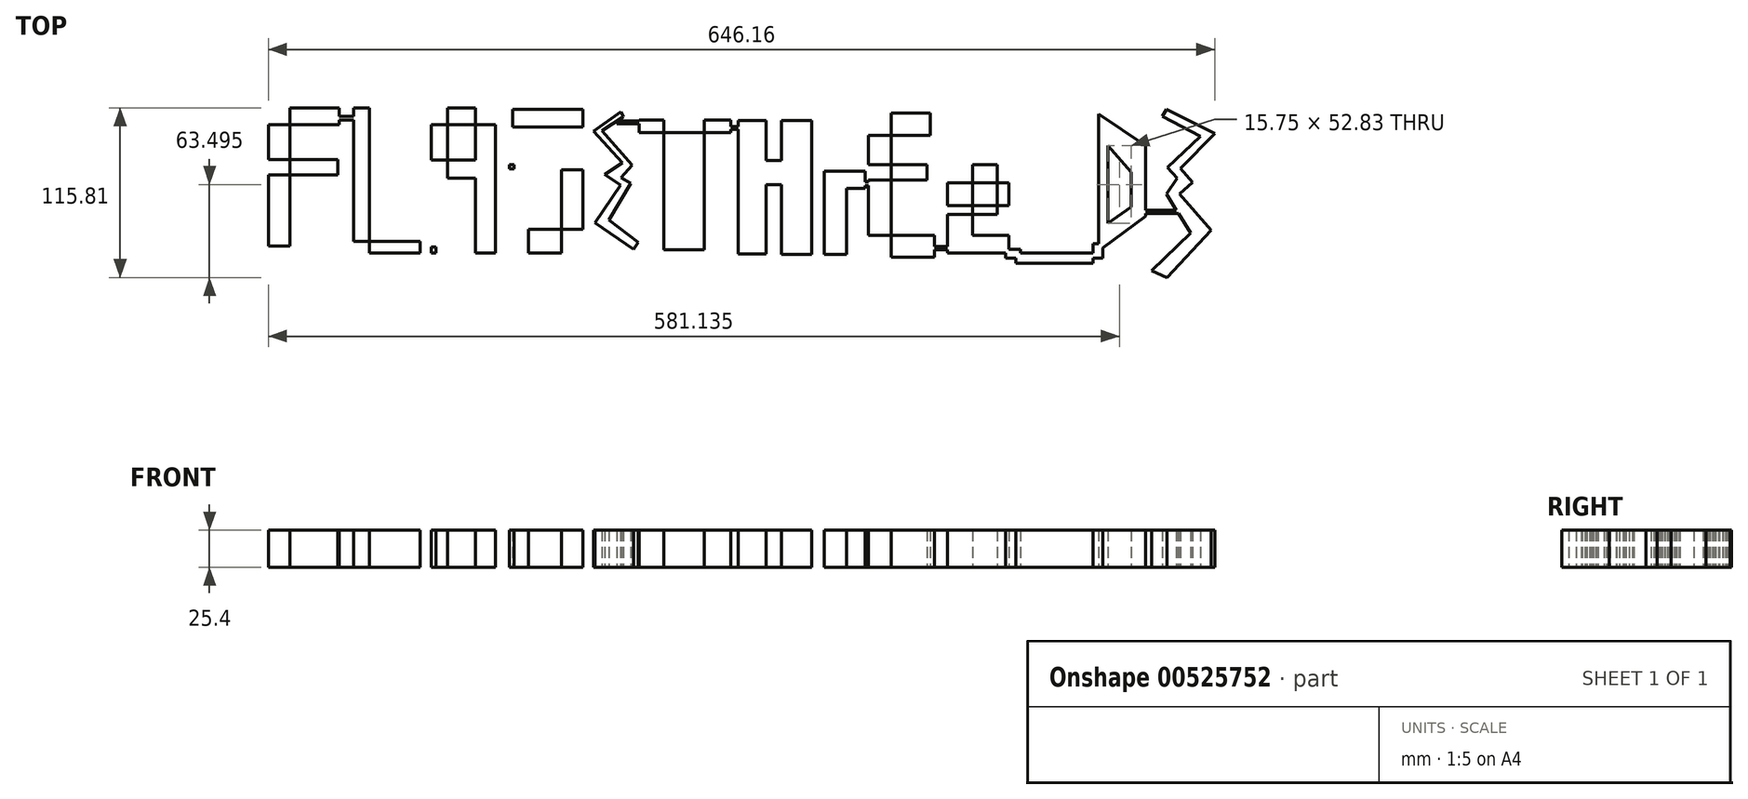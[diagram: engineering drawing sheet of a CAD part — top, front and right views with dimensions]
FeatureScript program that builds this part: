
annotation { "Feature Type Name" : "Feature", "Feature Type Description" : "" }
export const myFeature = defineFeature(function(context is Context, id is Id, definition is map)
    precondition{}
    {
        {
            var Q0;
            Q0=qCreatedBy(makeId("Top.planeOp"),FACE);
            var sketch = newSketch(context, id + "F0", { "sketchPlane" : qUnion([Q0])});
            skLineSegment(sketch, "E0.bottom", {"start": v(-64.83, -35.83) * mm, "end": v(-49.93, -35.83) * mm});
            skLineSegment(sketch, "E0.top", {"start": v(-64.83, 58.64) * mm, "end": v(-49.93, 58.64) * mm});
            skLineSegment(sketch, "E0.left", {"start": v(-64.83, -35.83) * mm, "end": v(-64.83, 58.64) * mm});
            skLineSegment(sketch, "E0.right", {"start": v(-49.93, -35.83) * mm, "end": v(-49.93, 58.64) * mm});
            skLineSegment(sketch, "E1.bottom", {"start": v(-64.83, 58.64) * mm, "end": v(-16.34, 58.64) * mm});
            skLineSegment(sketch, "E1.top", {"start": v(-64.83, 47.14) * mm, "end": v(-16.34, 47.14) * mm});
            skLineSegment(sketch, "E1.left", {"start": v(-64.83, 58.64) * mm, "end": v(-64.83, 47.14) * mm});
            skLineSegment(sketch, "E1.right", {"start": v(-16.34, 58.64) * mm, "end": v(-16.34, 47.14) * mm});
            skLineSegment(sketch, "E2.bottom", {"start": v(-64.83, 23.44) * mm, "end": v(-17.24, 23.44) * mm});
            skLineSegment(sketch, "E2.top", {"start": v(-64.83, 12.84) * mm, "end": v(-17.24, 12.84) * mm});
            skLineSegment(sketch, "E2.left", {"start": v(-64.83, 23.44) * mm, "end": v(-64.83, 12.84) * mm});
            skLineSegment(sketch, "E2.right", {"start": v(-17.24, 23.44) * mm, "end": v(-17.24, 12.84) * mm});
            skLineSegment(sketch, "E3.bottom", {"start": v(-6.65, 58.64) * mm, "end": v(4.31, 58.64) * mm});
            skLineSegment(sketch, "E3.top", {"start": v(-6.65, -40.32) * mm, "end": v(4.31, -40.32) * mm});
            skLineSegment(sketch, "E3.left", {"start": v(-6.65, 58.64) * mm, "end": v(-6.65, -40.32) * mm});
            skLineSegment(sketch, "E3.right", {"start": v(4.31, 58.64) * mm, "end": v(4.31, -40.32) * mm});
            skLineSegment(sketch, "E4.bottom", {"start": v(-6.65, -40.32) * mm, "end": v(38.97, -40.32) * mm});
            skLineSegment(sketch, "E4.top", {"start": v(-6.65, -32.6) * mm, "end": v(38.97, -32.6) * mm});
            skLineSegment(sketch, "E4.left", {"start": v(-6.65, -40.32) * mm, "end": v(-6.65, -32.6) * mm});
            skLineSegment(sketch, "E4.right", {"start": v(38.97, -40.32) * mm, "end": v(38.97, -32.6) * mm});
            skLineSegment(sketch, "E5.bottom", {"start": v(46.34, -40.32) * mm, "end": v(57.47, -40.32) * mm});
            skLineSegment(sketch, "E5.top", {"start": v(46.34, 58.64) * mm, "end": v(57.47, 58.64) * mm});
            skLineSegment(sketch, "E5.left", {"start": v(46.34, -40.32) * mm, "end": v(46.34, 58.64) * mm});
            skLineSegment(sketch, "E5.right", {"start": v(57.47, -40.32) * mm, "end": v(57.47, 58.64) * mm});
            skLineSegment(sketch, "E6.bottom", {"start": v(46.34, 58.64) * mm, "end": v(90.34, 58.64) * mm});
            skLineSegment(sketch, "E6.top", {"start": v(46.34, 47.32) * mm, "end": v(90.34, 47.32) * mm});
            skLineSegment(sketch, "E6.left", {"start": v(46.34, 58.64) * mm, "end": v(46.34, 47.32) * mm});
            skLineSegment(sketch, "E6.right", {"start": v(90.34, 58.64) * mm, "end": v(90.34, 47.32) * mm});
            skLineSegment(sketch, "E7.bottom", {"start": v(90.34, 58.64) * mm, "end": v(76.5, 58.64) * mm});
            skLineSegment(sketch, "E7.top", {"start": v(90.34, -40.32) * mm, "end": v(76.5, -40.32) * mm});
            skLineSegment(sketch, "E7.left", {"start": v(90.34, 58.64) * mm, "end": v(90.34, -40.32) * mm});
            skLineSegment(sketch, "E7.right", {"start": v(76.5, 58.64) * mm, "end": v(76.5, -40.32) * mm});
            skLineSegment(sketch, "E8.bottom", {"start": v(46.34, 23.08) * mm, "end": v(90.34, 23.08) * mm});
            skLineSegment(sketch, "E8.top", {"start": v(46.34, 10.69) * mm, "end": v(90.34, 10.69) * mm});
            skLineSegment(sketch, "E8.left", {"start": v(46.34, 23.08) * mm, "end": v(46.34, 10.69) * mm});
            skLineSegment(sketch, "E8.right", {"start": v(90.34, 23.08) * mm, "end": v(90.34, 10.69) * mm});
            skLineSegment(sketch, "E9.bottom", {"start": v(99.74, 57.74) * mm, "end": v(112.67, 57.74) * mm});
            skLineSegment(sketch, "E9.top", {"start": v(99.74, -40.5) * mm, "end": v(112.67, -40.5) * mm});
            skLineSegment(sketch, "E9.left", {"start": v(99.74, 57.74) * mm, "end": v(99.74, -40.5) * mm});
            skLineSegment(sketch, "E9.right", {"start": v(112.67, 57.74) * mm, "end": v(112.67, -40.5) * mm});
            skLineSegment(sketch, "E10.bottom", {"start": v(99.74, -40.5) * mm, "end": v(149.85, -40.5) * mm});
            skLineSegment(sketch, "E10.top", {"start": v(99.74, -24.16) * mm, "end": v(149.85, -24.16) * mm});
            skLineSegment(sketch, "E10.left", {"start": v(99.74, -40.5) * mm, "end": v(99.74, -24.16) * mm});
            skLineSegment(sketch, "E10.right", {"start": v(149.85, -40.5) * mm, "end": v(149.85, -24.16) * mm});
            skLineSegment(sketch, "E11.bottom", {"start": v(149.85, -40.5) * mm, "end": v(135.3, -40.5) * mm});
            skLineSegment(sketch, "E11.top", {"start": v(149.85, 16.43) * mm, "end": v(135.3, 16.43) * mm});
            skLineSegment(sketch, "E11.left", {"start": v(149.85, -40.5) * mm, "end": v(149.85, 16.43) * mm});
            skLineSegment(sketch, "E11.right", {"start": v(135.3, -40.5) * mm, "end": v(135.3, 16.43) * mm});
            skLineSegment(sketch, "E12.bottom", {"start": v(101.9, 57.74) * mm, "end": v(149.85, 57.74) * mm});
            skLineSegment(sketch, "E12.top", {"start": v(101.9, 45.7) * mm, "end": v(149.85, 45.7) * mm});
            skLineSegment(sketch, "E12.left", {"start": v(101.9, 57.74) * mm, "end": v(101.9, 45.7) * mm});
            skLineSegment(sketch, "E12.right", {"start": v(149.85, 57.74) * mm, "end": v(149.85, 45.7) * mm});
            skLineSegment(sketch, "E13", {"start": v(176.04, 56.16) * mm, "end": v(157.37, 42.57) * mm});
            skLineSegment(sketch, "E14", {"start": v(157.37, 42.57) * mm, "end": v(177.05, 20.98) * mm});
            skLineSegment(sketch, "E15", {"start": v(177.05, 20.98) * mm, "end": v(164.86, 13.11) * mm});
            skLineSegment(sketch, "E16", {"start": v(164.86, 13.11) * mm, "end": v(175.65, 5.74) * mm});
            skLineSegment(sketch, "E17", {"start": v(175.65, 5.74) * mm, "end": v(158.17, -19.88) * mm});
            skLineSegment(sketch, "E18", {"start": v(158.17, -19.88) * mm, "end": v(184.46, -37.82) * mm});
            skLineSegment(sketch, "E19", {"start": v(184.46, -37.82) * mm, "end": v(187.69, -33.1) * mm});
            skLineSegment(sketch, "E20", {"start": v(187.69, -33.1) * mm, "end": v(167.65, -17.88) * mm});
            skLineSegment(sketch, "E21", {"start": v(167.65, -17.88) * mm, "end": v(182.51, 7.27) * mm});
            skLineSegment(sketch, "E22", {"start": v(182.51, 7.27) * mm, "end": v(175.99, 11.12) * mm});
            skLineSegment(sketch, "E23", {"start": v(175.99, 11.12) * mm, "end": v(183.66, 19.59) * mm});
            skLineSegment(sketch, "E24", {"start": v(183.66, 19.59) * mm, "end": v(163.08, 42.95) * mm});
            skLineSegment(sketch, "E25", {"start": v(163.08, 42.95) * mm, "end": v(177.69, 52.6) * mm});
            skLineSegment(sketch, "E26", {"start": v(177.69, 52.6) * mm, "end": v(176.04, 56.16) * mm});
            skLineSegment(sketch, "E27.bottom", {"start": v(188.24, 50.3) * mm, "end": v(251.03, 50.3) * mm});
            skLineSegment(sketch, "E27.top", {"start": v(188.24, 41.76) * mm, "end": v(251.03, 41.76) * mm});
            skLineSegment(sketch, "E27.left", {"start": v(188.24, 50.3) * mm, "end": v(188.24, 41.76) * mm});
            skLineSegment(sketch, "E27.right", {"start": v(251.03, 50.3) * mm, "end": v(251.03, 41.76) * mm});
            skLineSegment(sketch, "E28.bottom", {"start": v(205.11, 50.3) * mm, "end": v(232.66, 50.3) * mm});
            skLineSegment(sketch, "E28.top", {"start": v(205.11, -38.33) * mm, "end": v(232.66, -38.33) * mm});
            skLineSegment(sketch, "E28.left", {"start": v(205.11, 50.3) * mm, "end": v(205.11, -38.33) * mm});
            skLineSegment(sketch, "E28.right", {"start": v(232.66, 50.3) * mm, "end": v(232.66, -38.33) * mm});
            skLineSegment(sketch, "E29.bottom", {"start": v(255.94, 49.88) * mm, "end": v(275.16, 49.88) * mm});
            skLineSegment(sketch, "E29.top", {"start": v(255.94, -41.1) * mm, "end": v(275.16, -41.1) * mm});
            skLineSegment(sketch, "E29.left", {"start": v(255.94, 49.88) * mm, "end": v(255.94, -41.1) * mm});
            skLineSegment(sketch, "E29.right", {"start": v(275.16, 49.88) * mm, "end": v(275.16, -41.1) * mm});
            skLineSegment(sketch, "E30.bottom", {"start": v(262.35, 22.75) * mm, "end": v(298.66, 22.75) * mm});
            skLineSegment(sketch, "E30.top", {"start": v(262.35, 6.3) * mm, "end": v(298.66, 6.3) * mm});
            skLineSegment(sketch, "E30.left", {"start": v(262.35, 22.75) * mm, "end": v(262.35, 6.3) * mm});
            skLineSegment(sketch, "E30.right", {"start": v(298.66, 22.75) * mm, "end": v(298.66, 6.3) * mm});
            skLineSegment(sketch, "E31.bottom", {"start": v(285.63, 50.1) * mm, "end": v(306.13, 50.1) * mm});
            skLineSegment(sketch, "E31.top", {"start": v(285.63, -41.53) * mm, "end": v(306.13, -41.53) * mm});
            skLineSegment(sketch, "E31.left", {"start": v(285.63, 50.1) * mm, "end": v(285.63, -41.53) * mm});
            skLineSegment(sketch, "E31.right", {"start": v(306.13, 50.1) * mm, "end": v(306.13, -41.53) * mm});
            skLineSegment(sketch, "E32.bottom", {"start": v(330.05, -41.53) * mm, "end": v(314.9, -41.53) * mm});
            skLineSegment(sketch, "E32.top", {"start": v(330.05, 15.28) * mm, "end": v(314.9, 15.28) * mm});
            skLineSegment(sketch, "E32.left", {"start": v(330.05, -41.53) * mm, "end": v(330.05, 15.28) * mm});
            skLineSegment(sketch, "E32.right", {"start": v(314.9, -41.53) * mm, "end": v(314.9, 15.28) * mm});
            skLineSegment(sketch, "E33.bottom", {"start": v(314.9, 15.28) * mm, "end": v(342.66, 15.28) * mm});
            skLineSegment(sketch, "E33.top", {"start": v(314.9, 3.53) * mm, "end": v(342.66, 3.53) * mm});
            skLineSegment(sketch, "E33.left", {"start": v(314.9, 15.28) * mm, "end": v(314.9, 3.53) * mm});
            skLineSegment(sketch, "E33.right", {"start": v(342.66, 15.28) * mm, "end": v(342.66, 3.53) * mm});
            skLineSegment(sketch, "E34.bottom", {"start": v(344.8, 55) * mm, "end": v(360.38, 55) * mm});
            skLineSegment(sketch, "E34.top", {"start": v(344.8, -43.46) * mm, "end": v(360.38, -43.46) * mm});
            skLineSegment(sketch, "E34.left", {"start": v(344.8, 55) * mm, "end": v(344.8, -43.46) * mm});
            skLineSegment(sketch, "E34.right", {"start": v(360.38, 55) * mm, "end": v(360.38, -43.46) * mm});
            skLineSegment(sketch, "E35.bottom", {"start": v(344.8, 55) * mm, "end": v(387.08, 55) * mm});
            skLineSegment(sketch, "E35.top", {"start": v(344.8, 39.84) * mm, "end": v(387.08, 39.84) * mm});
            skLineSegment(sketch, "E35.left", {"start": v(344.8, 55) * mm, "end": v(344.8, 39.84) * mm});
            skLineSegment(sketch, "E35.right", {"start": v(387.08, 55) * mm, "end": v(387.08, 39.84) * mm});
            skLineSegment(sketch, "E36.bottom", {"start": v(344.8, 19.76) * mm, "end": v(384.94, 19.76) * mm});
            skLineSegment(sketch, "E36.top", {"start": v(344.8, 9.51) * mm, "end": v(384.94, 9.51) * mm});
            skLineSegment(sketch, "E36.left", {"start": v(344.8, 19.76) * mm, "end": v(344.8, 9.51) * mm});
            skLineSegment(sketch, "E36.right", {"start": v(384.94, 19.76) * mm, "end": v(384.94, 9.51) * mm});
            skLineSegment(sketch, "E37.bottom", {"start": v(344.8, -43.46) * mm, "end": v(389.86, -43.46) * mm});
            skLineSegment(sketch, "E37.top", {"start": v(344.8, -28.3) * mm, "end": v(389.86, -28.3) * mm});
            skLineSegment(sketch, "E37.left", {"start": v(344.8, -43.46) * mm, "end": v(344.8, -28.3) * mm});
            skLineSegment(sketch, "E37.right", {"start": v(389.86, -43.46) * mm, "end": v(389.86, -28.3) * mm});
            skLineSegment(sketch, "E38.bottom", {"start": v(415.91, -40.47) * mm, "end": v(398.83, -40.47) * mm});
            skLineSegment(sketch, "E38.top", {"start": v(415.91, 19.76) * mm, "end": v(398.83, 19.76) * mm});
            skLineSegment(sketch, "E38.left", {"start": v(415.91, -40.47) * mm, "end": v(415.91, 19.76) * mm});
            skLineSegment(sketch, "E38.right", {"start": v(398.83, -40.47) * mm, "end": v(398.83, 19.76) * mm});
            skLineSegment(sketch, "E39.bottom", {"start": v(398.83, 19.76) * mm, "end": v(440.9, 19.76) * mm});
            skLineSegment(sketch, "E39.top", {"start": v(398.83, 7.59) * mm, "end": v(440.9, 7.59) * mm});
            skLineSegment(sketch, "E39.left", {"start": v(398.83, 19.76) * mm, "end": v(398.83, 7.59) * mm});
            skLineSegment(sketch, "E39.right", {"start": v(440.9, 19.76) * mm, "end": v(440.9, 7.59) * mm});
            skLineSegment(sketch, "E40.bottom", {"start": v(440.9, 19.76) * mm, "end": v(432.78, 19.76) * mm});
            skLineSegment(sketch, "E40.top", {"start": v(440.9, -13.98) * mm, "end": v(432.78, -13.98) * mm});
            skLineSegment(sketch, "E40.left", {"start": v(440.9, 19.76) * mm, "end": v(440.9, -13.98) * mm});
            skLineSegment(sketch, "E40.right", {"start": v(432.78, 19.76) * mm, "end": v(432.78, -13.98) * mm});
            skLineSegment(sketch, "E41.bottom", {"start": v(440.9, -13.98) * mm, "end": v(398.83, -13.98) * mm});
            skLineSegment(sketch, "E41.top", {"start": v(440.9, -8) * mm, "end": v(398.83, -8) * mm});
            skLineSegment(sketch, "E41.left", {"start": v(440.9, -13.98) * mm, "end": v(440.9, -8) * mm});
            skLineSegment(sketch, "E41.right", {"start": v(398.83, -13.98) * mm, "end": v(398.83, -8) * mm});
            skLineSegment(sketch, "E42.bottom", {"start": v(398.83, -40.47) * mm, "end": v(440.9, -40.47) * mm});
            skLineSegment(sketch, "E42.top", {"start": v(398.83, -28.3) * mm, "end": v(440.9, -28.3) * mm});
            skLineSegment(sketch, "E42.left", {"start": v(398.83, -40.47) * mm, "end": v(398.83, -28.3) * mm});
            skLineSegment(sketch, "E42.right", {"start": v(440.9, -40.47) * mm, "end": v(440.9, -28.3) * mm});
            skPoint(sketch, "E43.firstSnap0", {"position": v(419.86, -40.47) * mm});
            skLineSegment(sketch, "E43.bottom", {"start": v(445.44, -40.47) * mm, "end": v(498.27, -40.47) * mm});
            skLineSegment(sketch, "E43.top", {"start": v(445.44, -47.52) * mm, "end": v(498.27, -47.52) * mm});
            skLineSegment(sketch, "E43.left", {"start": v(445.44, -40.47) * mm, "end": v(445.44, -47.52) * mm});
            skLineSegment(sketch, "E43.right", {"start": v(498.27, -40.47) * mm, "end": v(498.27, -47.52) * mm});
            skLineSegment(sketch, "E44", {"start": v(502.08, -39.14) * mm, "end": v(502.08, 54.33) * mm});
            skLineSegment(sketch, "E45", {"start": v(502.08, 54.33) * mm, "end": v(534.08, 32.74) * mm});
            skLineSegment(sketch, "E46", {"start": v(534.08, 32.74) * mm, "end": v(534.08, -15.52) * mm});
            skLineSegment(sketch, "E47", {"start": v(534.08, -15.52) * mm, "end": v(502.08, -39.14) * mm});
            skLineSegment(sketch, "E48", {"start": v(508.43, -20.09) * mm, "end": v(508.43, 32.74) * mm});
            skLineSegment(sketch, "E49", {"start": v(508.43, 32.74) * mm, "end": v(524.18, 14.7) * mm});
            skLineSegment(sketch, "E50", {"start": v(524.18, 14.7) * mm, "end": v(524.18, -8.91) * mm});
            skLineSegment(sketch, "E51", {"start": v(508.43, -20.09) * mm, "end": v(524.18, -8.91) * mm});
            skLineSegment(sketch, "E52", {"start": v(545.51, 52.8) * mm, "end": v(571.67, 39.34) * mm});
            skLineSegment(sketch, "E53", {"start": v(571.67, 39.34) * mm, "end": v(549.07, 18) * mm});
            skLineSegment(sketch, "E54", {"start": v(549.07, 18) * mm, "end": v(555.86, 10.8) * mm});
            skLineSegment(sketch, "E55", {"start": v(555.86, 10.8) * mm, "end": v(548.3, 0) * mm});
            skLineSegment(sketch, "E56", {"start": v(548.3, 0) * mm, "end": v(564.82, -26.95) * mm});
            skLineSegment(sketch, "E57", {"start": v(564.82, -26.95) * mm, "end": v(538.4, -52.6) * mm});
            skLineSegment(sketch, "E58", {"start": v(538.4, -52.6) * mm, "end": v(548.82, -57.17) * mm});
            skLineSegment(sketch, "E59", {"start": v(548.82, -57.17) * mm, "end": v(579.04, -24.92) * mm});
            skLineSegment(sketch, "E60", {"start": v(579.04, -24.92) * mm, "end": v(557.45, 0) * mm});
            skLineSegment(sketch, "E61", {"start": v(557.45, 0) * mm, "end": v(566.3, 7.67) * mm});
            skLineSegment(sketch, "E62", {"start": v(566.3, 7.67) * mm, "end": v(557.83, 17.46) * mm});
            skLineSegment(sketch, "E63", {"start": v(557.83, 17.46) * mm, "end": v(581.33, 41.12) * mm});
            skLineSegment(sketch, "E64", {"start": v(581.33, 41.12) * mm, "end": v(548.56, 57.63) * mm});
            skLineSegment(sketch, "E65", {"start": v(548.56, 57.63) * mm, "end": v(545.51, 52.8) * mm});
            skPoint(sketch, "E66.firstSnap0", {"position": v(-16.34, 52.9) * mm});
            skLineSegment(sketch, "E66.bottom", {"start": v(-19.12, 52.9) * mm, "end": v(-3.22, 52.9) * mm});
            skLineSegment(sketch, "E66.top", {"start": v(-19.12, 50.27) * mm, "end": v(-3.22, 50.27) * mm});
            skLineSegment(sketch, "E66.left", {"start": v(-19.12, 52.9) * mm, "end": v(-19.12, 50.27) * mm});
            skLineSegment(sketch, "E66.right", {"start": v(-3.22, 52.9) * mm, "end": v(-3.22, 50.27) * mm});
            skLineSegment(sketch, "E67.bottom", {"start": v(38.97, -36.46) * mm, "end": v(49.7, -36.46) * mm});
            skLineSegment(sketch, "E67.top", {"start": v(38.97, -40.32) * mm, "end": v(49.7, -40.32) * mm});
            skLineSegment(sketch, "E67.left", {"start": v(38.97, -36.46) * mm, "end": v(38.97, -40.32) * mm});
            skLineSegment(sketch, "E67.right", {"start": v(49.7, -36.46) * mm, "end": v(49.7, -40.32) * mm});
            skLineSegment(sketch, "E68.bottom", {"start": v(87.25, 19.77) * mm, "end": v(102.9, 19.77) * mm});
            skLineSegment(sketch, "E68.top", {"start": v(87.25, 16.9) * mm, "end": v(102.9, 16.9) * mm});
            skLineSegment(sketch, "E68.left", {"start": v(87.25, 19.77) * mm, "end": v(87.25, 16.9) * mm});
            skLineSegment(sketch, "E68.right", {"start": v(102.9, 19.77) * mm, "end": v(102.9, 16.9) * mm});
            skLineSegment(sketch, "E69.bottom", {"start": v(149.85, -18.56) * mm, "end": v(163.12, -18.56) * mm});
            skLineSegment(sketch, "E69.top", {"start": v(149.85, -20.12) * mm, "end": v(163.12, -20.12) * mm});
            skLineSegment(sketch, "E69.left", {"start": v(149.85, -18.56) * mm, "end": v(149.85, -20.12) * mm});
            skLineSegment(sketch, "E69.right", {"start": v(163.12, -18.56) * mm, "end": v(163.12, -20.12) * mm});
            skPoint(sketch, "E70.oppositeSnap0", {"position": v(170.38, 47.78) * mm});
            skLineSegment(sketch, "E70.bottom", {"start": v(173.25, 49.67) * mm, "end": v(192.06, 49.67) * mm});
            skLineSegment(sketch, "E70.top", {"start": v(173.25, 47.78) * mm, "end": v(192.06, 47.78) * mm});
            skLineSegment(sketch, "E70.left", {"start": v(173.25, 49.67) * mm, "end": v(173.25, 47.78) * mm});
            skLineSegment(sketch, "E70.right", {"start": v(192.06, 49.67) * mm, "end": v(192.06, 47.78) * mm});
            skPoint(sketch, "E71.firstSnap0", {"position": v(188.24, 46.03) * mm});
            skLineSegment(sketch, "E71.bottom", {"start": v(248.37, 46.03) * mm, "end": v(259.32, 46.03) * mm});
            skLineSegment(sketch, "E71.top", {"start": v(248.37, 44.01) * mm, "end": v(259.32, 44.01) * mm});
            skLineSegment(sketch, "E71.left", {"start": v(248.37, 46.03) * mm, "end": v(248.37, 44.01) * mm});
            skLineSegment(sketch, "E71.right", {"start": v(259.32, 46.03) * mm, "end": v(259.32, 44.01) * mm});
            skLineSegment(sketch, "E72.bottom", {"start": v(306.13, 9.6) * mm, "end": v(319.03, 9.6) * mm});
            skLineSegment(sketch, "E72.top", {"start": v(306.13, 7.51) * mm, "end": v(319.03, 7.51) * mm});
            skLineSegment(sketch, "E72.left", {"start": v(306.13, 9.6) * mm, "end": v(306.13, 7.51) * mm});
            skLineSegment(sketch, "E72.right", {"start": v(319.03, 9.6) * mm, "end": v(319.03, 7.51) * mm});
            skLineSegment(sketch, "E73.bottom", {"start": v(339.1, 8.04) * mm, "end": v(352.14, 8.04) * mm});
            skLineSegment(sketch, "E73.top", {"start": v(339.1, 5.43) * mm, "end": v(352.14, 5.43) * mm});
            skLineSegment(sketch, "E73.left", {"start": v(339.1, 8.04) * mm, "end": v(339.1, 5.43) * mm});
            skLineSegment(sketch, "E73.right", {"start": v(352.14, 8.04) * mm, "end": v(352.14, 5.43) * mm});
            skPoint(sketch, "E74.firstSnap0", {"position": v(389.86, -35.87) * mm});
            skLineSegment(sketch, "E74.bottom", {"start": v(386.55, -35.87) * mm, "end": v(404.8, -35.87) * mm});
            skLineSegment(sketch, "E74.top", {"start": v(386.55, -38.37) * mm, "end": v(404.8, -38.37) * mm});
            skLineSegment(sketch, "E74.left", {"start": v(386.55, -35.87) * mm, "end": v(386.55, -38.37) * mm});
            skLineSegment(sketch, "E74.right", {"start": v(404.8, -35.87) * mm, "end": v(404.8, -38.37) * mm});
            skPoint(sketch, "E75.oppositeSnap0", {"position": v(445.44, -44) * mm});
            skLineSegment(sketch, "E75.bottom", {"start": v(438.7, -37.85) * mm, "end": v(448.86, -37.85) * mm});
            skLineSegment(sketch, "E75.top", {"start": v(438.7, -44) * mm, "end": v(448.86, -44) * mm});
            skLineSegment(sketch, "E75.left", {"start": v(438.7, -37.85) * mm, "end": v(438.7, -44) * mm});
            skLineSegment(sketch, "E75.right", {"start": v(448.86, -37.85) * mm, "end": v(448.86, -44) * mm});
            skLineSegment(sketch, "E76.bottom", {"start": v(498.27, -44) * mm, "end": v(504.92, -44) * mm});
            skLineSegment(sketch, "E76.top", {"start": v(498.27, -34.2) * mm, "end": v(504.92, -34.2) * mm});
            skLineSegment(sketch, "E76.left", {"start": v(498.27, -44) * mm, "end": v(498.27, -34.2) * mm});
            skLineSegment(sketch, "E76.right", {"start": v(504.92, -44) * mm, "end": v(504.92, -34.2) * mm});
            skPoint(sketch, "E77.oppositeSnap0", {"position": v(556.56, -13.47) * mm});
            skLineSegment(sketch, "E77.bottom", {"start": v(530.99, -11.26) * mm, "end": v(561.5, -11.26) * mm});
            skLineSegment(sketch, "E77.top", {"start": v(530.99, -13.47) * mm, "end": v(561.5, -13.47) * mm});
            skLineSegment(sketch, "E77.left", {"start": v(530.99, -11.26) * mm, "end": v(530.99, -13.47) * mm});
            skLineSegment(sketch, "E77.right", {"start": v(561.5, -11.26) * mm, "end": v(561.5, -13.47) * mm});
            skSolve(sketch);
        }
        {
            var Q0;
            Q0=makeQuery(id+"F0.imprint","IMPRINT",FACE,{"disambiguationData":[TD([[makeQuery(id+"F0.imprint","IMPRINT",EDGE,{"derivedFrom":sQuery(id+"F0.wireOp",EDGE,"E52")}),1.0]])]});
            var Q1;
            {var subQ5=sQuery(id+"F0.wireOp",EDGE,"E77.right");Q1=makeQuery(id+"F0.imprint","IMPRINT",FACE,{"disambiguationData":[TD([[makeQuery(id+"F0.imprint","IMPRINT",EDGE,{"derivedFrom":subQ5}),-1.0]])]});}
            var Q2;
            {var subQ0=sQuery(id+"F0.wireOp",EDGE,"E77.bottom");var subQ1=sQuery(id+"F0.wireOp",EDGE,"E46");var subQ2=makeQuery(id+"F0.imprint","INTERSECT",VERTEX,{"derivedFrom":[subQ1,subQ0]});Q2=makeQuery(id+"F0.imprint","IMPRINT",FACE,{"disambiguationData":[TD([[makeQuery(id+"F0.imprint","IMPRINT",EDGE,{"disambiguationData":[TD([[subQ2,-1.0]])],"derivedFrom":subQ1}),1.0]])]});}
            var Q3;
            {var subQ5=sQuery(id+"F0.wireOp",EDGE,"E77.left");Q3=makeQuery(id+"F0.imprint","IMPRINT",FACE,{"disambiguationData":[TD([[makeQuery(id+"F0.imprint","IMPRINT",EDGE,{"derivedFrom":subQ5}),1.0]])]});}
            var Q4;
            {var subQ9=sQuery(id+"F0.wireOp",EDGE,"E45");Q4=makeQuery(id+"F0.imprint","IMPRINT",FACE,{"disambiguationData":[TD([[makeQuery(id+"F0.imprint","IMPRINT",EDGE,{"derivedFrom":subQ9}),-1.0]])]});}
            var Q5;
            {var subQ0=sQuery(id+"F0.wireOp",EDGE,"E47");var subQ1=sQuery(id+"F0.wireOp",EDGE,"E44");var subQ2=makeQuery(id+"F0.imprint","INTERSECT",VERTEX,{"derivedFrom":[subQ1,subQ0]});Q5=makeQuery(id+"F0.imprint","IMPRINT",FACE,{"disambiguationData":[TD([[makeQuery(id+"F0.imprint","IMPRINT",EDGE,{"disambiguationData":[TD([[subQ2,-1.0]])],"derivedFrom":subQ1}),-1.0]])]});}
            var Q6;
            {var subQ9=sQuery(id+"F0.wireOp",EDGE,"E76.bottom");Q6=makeQuery(id+"F0.imprint","IMPRINT",FACE,{"disambiguationData":[TD([[makeQuery(id+"F0.imprint","IMPRINT",EDGE,{"derivedFrom":subQ9}),1.0]])]});}
            var Q7;
            {var subQ2=sQuery(id+"F0.wireOp",EDGE,"E43.top");Q7=makeQuery(id+"F0.imprint","IMPRINT",FACE,{"disambiguationData":[TD([[makeQuery(id+"F0.imprint","IMPRINT",EDGE,{"derivedFrom":subQ2}),1.0]])]});}
            var Q8;
            {var subQ0=sQuery(id+"F0.wireOp",EDGE,"E43.left");var subQ1=sQuery(id+"F0.wireOp",EDGE,"E43.bottom");var subQ2=makeQuery(id+"F0.imprint","INTERSECT",VERTEX,{"derivedFrom":[subQ1,subQ0]});Q8=makeQuery(id+"F0.imprint","IMPRINT",FACE,{"disambiguationData":[TD([[makeQuery(id+"F0.imprint","IMPRINT",EDGE,{"disambiguationData":[TD([[subQ2,-1.0]])],"derivedFrom":subQ1}),-1.0]])]});}
            var Q9;
            {var subQ7=sQuery(id+"F0.wireOp",EDGE,"E42.right");var subQ11=sQuery(id+"F0.wireOp",EDGE,"E42.bottom");var subQ12=makeQuery(id+"F0.imprint","INTERSECT",VERTEX,{"derivedFrom":[subQ11,subQ7]});Q9=makeQuery(id+"F0.imprint","IMPRINT",FACE,{"disambiguationData":[TD([[makeQuery(id+"F0.imprint","IMPRINT",EDGE,{"disambiguationData":[TD([[subQ12,1.0]])],"derivedFrom":subQ11}),-1.0]])]});}
            var Q10;
            {var subQ0=sQuery(id+"F0.wireOp",EDGE,"E42.right");var subQ1=sQuery(id+"F0.wireOp",EDGE,"E42.bottom");var subQ2=makeQuery(id+"F0.imprint","INTERSECT",VERTEX,{"derivedFrom":[subQ1,subQ0]});Q10=makeQuery(id+"F0.imprint","IMPRINT",FACE,{"disambiguationData":[TD([[makeQuery(id+"F0.imprint","IMPRINT",EDGE,{"disambiguationData":[TD([[subQ2,1.0]])],"derivedFrom":subQ1}),1.0]])]});}
            var Q11;
            {var subQ7=sQuery(id+"F0.wireOp",EDGE,"E38.left");var subQ9=sQuery(id+"F0.wireOp",EDGE,"E42.bottom");var subQ10=makeQuery(id+"F0.imprint","INTERSECT",VERTEX,{"derivedFrom":[subQ7,subQ9]});Q11=makeQuery(id+"F0.imprint","IMPRINT",FACE,{"disambiguationData":[TD([[makeQuery(id+"F0.imprint","IMPRINT",EDGE,{"disambiguationData":[TD([[subQ10,-1.0]])],"derivedFrom":subQ7}),-1.0]])]});}
            var Q12;
            {var subQ10=sQuery(id+"F0.wireOp",EDGE,"E74.right");Q12=makeQuery(id+"F0.imprint","IMPRINT",FACE,{"disambiguationData":[TD([[makeQuery(id+"F0.imprint","IMPRINT",EDGE,{"derivedFrom":subQ10}),1.0]])]});}
            var Q13;
            {var subQ5=sQuery(id+"F0.wireOp",EDGE,"E74.right");Q13=makeQuery(id+"F0.imprint","IMPRINT",FACE,{"disambiguationData":[TD([[makeQuery(id+"F0.imprint","IMPRINT",EDGE,{"derivedFrom":subQ5}),-1.0]])]});}
            var Q14;
            {var subQ0=sQuery(id+"F0.wireOp",EDGE,"E42.top");var subQ1=sQuery(id+"F0.wireOp",EDGE,"E38.left");var subQ2=makeQuery(id+"F0.imprint","INTERSECT",VERTEX,{"derivedFrom":[subQ1,subQ0]});Q14=makeQuery(id+"F0.imprint","IMPRINT",FACE,{"disambiguationData":[TD([[makeQuery(id+"F0.imprint","IMPRINT",EDGE,{"disambiguationData":[TD([[subQ2,-1.0]])],"derivedFrom":subQ1}),1.0]])]});}
            var Q15;
            {var subQ5=sQuery(id+"F0.wireOp",EDGE,"E41.right");Q15=makeQuery(id+"F0.imprint","IMPRINT",FACE,{"disambiguationData":[TD([[makeQuery(id+"F0.imprint","IMPRINT",EDGE,{"derivedFrom":subQ5}),-1.0]])]});}
            var Q16;
            {var subQ0=sQuery(id+"F0.wireOp",EDGE,"E41.bottom");var subQ1=sQuery(id+"F0.wireOp",EDGE,"E38.left");var subQ2=makeQuery(id+"F0.imprint","INTERSECT",VERTEX,{"derivedFrom":[subQ1,subQ0]});Q16=makeQuery(id+"F0.imprint","IMPRINT",FACE,{"disambiguationData":[TD([[makeQuery(id+"F0.imprint","IMPRINT",EDGE,{"disambiguationData":[TD([[subQ2,-1.0]])],"derivedFrom":subQ1}),-1.0]])]});}
            var Q17;
            {var subQ5=sQuery(id+"F0.wireOp",EDGE,"E41.left");Q17=makeQuery(id+"F0.imprint","IMPRINT",FACE,{"disambiguationData":[TD([[makeQuery(id+"F0.imprint","IMPRINT",EDGE,{"derivedFrom":subQ5}),1.0]])]});}
            var Q18;
            {var subQ0=sQuery(id+"F0.wireOp",EDGE,"E40.left");var subQ1=sQuery(id+"F0.wireOp",EDGE,"E39.top");var subQ2=makeQuery(id+"F0.imprint","INTERSECT",VERTEX,{"derivedFrom":[subQ1,subQ0]});Q18=makeQuery(id+"F0.imprint","IMPRINT",FACE,{"disambiguationData":[TD([[makeQuery(id+"F0.imprint","IMPRINT",EDGE,{"disambiguationData":[TD([[subQ2,1.0]])],"derivedFrom":subQ1}),-1.0]])]});}
            var Q19;
            {var subQ5=sQuery(id+"F0.wireOp",EDGE,"E40.bottom");Q19=makeQuery(id+"F0.imprint","IMPRINT",FACE,{"disambiguationData":[TD([[makeQuery(id+"F0.imprint","IMPRINT",EDGE,{"derivedFrom":subQ5}),1.0]])]});}
            var Q20;
            {var subQ0=sQuery(id+"F0.wireOp",EDGE,"E39.bottom");var subQ1=sQuery(id+"F0.wireOp",EDGE,"E38.left");var subQ2=makeQuery(id+"F0.imprint","INTERSECT",VERTEX,{"derivedFrom":[subQ1,subQ0]});Q20=makeQuery(id+"F0.imprint","IMPRINT",FACE,{"disambiguationData":[TD([[makeQuery(id+"F0.imprint","IMPRINT",EDGE,{"disambiguationData":[TD([[subQ2,1.0]])],"derivedFrom":subQ1}),-1.0]])]});}
            var Q21;
            {var subQ5=sQuery(id+"F0.wireOp",EDGE,"E39.left");Q21=makeQuery(id+"F0.imprint","IMPRINT",FACE,{"disambiguationData":[TD([[makeQuery(id+"F0.imprint","IMPRINT",EDGE,{"derivedFrom":subQ5}),1.0]])]});}
            var Q22;
            {var subQ0=sQuery(id+"F0.wireOp",EDGE,"E41.top");var subQ1=sQuery(id+"F0.wireOp",EDGE,"E38.left");var subQ2=makeQuery(id+"F0.imprint","INTERSECT",VERTEX,{"derivedFrom":[subQ1,subQ0]});Q22=makeQuery(id+"F0.imprint","IMPRINT",FACE,{"disambiguationData":[TD([[makeQuery(id+"F0.imprint","IMPRINT",EDGE,{"disambiguationData":[TD([[subQ2,-1.0]])],"derivedFrom":subQ1}),1.0]])]});}
            var Q23;
            {var subQ0=sQuery(id+"F0.wireOp",EDGE,"E74.top");var subQ1=sQuery(id+"F0.wireOp",EDGE,"E37.right");var subQ2=makeQuery(id+"F0.imprint","INTERSECT",VERTEX,{"derivedFrom":[subQ1,subQ0]});Q23=makeQuery(id+"F0.imprint","IMPRINT",FACE,{"disambiguationData":[TD([[makeQuery(id+"F0.imprint","IMPRINT",EDGE,{"disambiguationData":[TD([[subQ2,-1.0]])],"derivedFrom":subQ1}),-1.0]])]});}
            var Q24;
            {var subQ5=sQuery(id+"F0.wireOp",EDGE,"E74.left");Q24=makeQuery(id+"F0.imprint","IMPRINT",FACE,{"disambiguationData":[TD([[makeQuery(id+"F0.imprint","IMPRINT",EDGE,{"derivedFrom":subQ5}),1.0]])]});}
            var Q25;
            {var subQ9=sQuery(id+"F0.wireOp",EDGE,"E74.left");Q25=makeQuery(id+"F0.imprint","IMPRINT",FACE,{"disambiguationData":[TD([[makeQuery(id+"F0.imprint","IMPRINT",EDGE,{"derivedFrom":subQ9}),-1.0]])]});}
            var Q26;
            {var subQ5=sQuery(id+"F0.wireOp",EDGE,"E37.left");Q26=makeQuery(id+"F0.imprint","IMPRINT",FACE,{"disambiguationData":[TD([[makeQuery(id+"F0.imprint","IMPRINT",EDGE,{"derivedFrom":subQ5}),-1.0]])]});}
            var Q27;
            {var subQ7=sQuery(id+"F0.wireOp",EDGE,"E73.right");Q27=makeQuery(id+"F0.imprint","IMPRINT",FACE,{"disambiguationData":[TD([[makeQuery(id+"F0.imprint","IMPRINT",EDGE,{"derivedFrom":subQ7}),1.0]])]});}
            var Q28;
            {var subQ5=sQuery(id+"F0.wireOp",EDGE,"E36.left");Q28=makeQuery(id+"F0.imprint","IMPRINT",FACE,{"disambiguationData":[TD([[makeQuery(id+"F0.imprint","IMPRINT",EDGE,{"derivedFrom":subQ5}),1.0]])]});}
            var Q29;
            {var subQ5=sQuery(id+"F0.wireOp",EDGE,"E36.right");Q29=makeQuery(id+"F0.imprint","IMPRINT",FACE,{"disambiguationData":[TD([[makeQuery(id+"F0.imprint","IMPRINT",EDGE,{"derivedFrom":subQ5}),-1.0]])]});}
            var Q30;
            {var subQ0=sQuery(id+"F0.wireOp",EDGE,"E35.top");var subQ5=sQuery(id+"F0.wireOp",EDGE,"E34.right");var subQ6=makeQuery(id+"F0.imprint","INTERSECT",VERTEX,{"derivedFrom":[subQ5,subQ0]});Q30=makeQuery(id+"F0.imprint","IMPRINT",FACE,{"disambiguationData":[TD([[makeQuery(id+"F0.imprint","IMPRINT",EDGE,{"disambiguationData":[TD([[subQ6,-1.0]])],"derivedFrom":subQ5}),-1.0]])]});}
            var Q31;
            {var subQ5=sQuery(id+"F0.wireOp",EDGE,"E35.left");Q31=makeQuery(id+"F0.imprint","IMPRINT",FACE,{"disambiguationData":[TD([[makeQuery(id+"F0.imprint","IMPRINT",EDGE,{"derivedFrom":subQ5}),1.0]])]});}
            var Q32;
            {var subQ5=sQuery(id+"F0.wireOp",EDGE,"E35.right");Q32=makeQuery(id+"F0.imprint","IMPRINT",FACE,{"disambiguationData":[TD([[makeQuery(id+"F0.imprint","IMPRINT",EDGE,{"derivedFrom":subQ5}),-1.0]])]});}
            var Q33;
            {var subQ5=sQuery(id+"F0.wireOp",EDGE,"E73.right");Q33=makeQuery(id+"F0.imprint","IMPRINT",FACE,{"disambiguationData":[TD([[makeQuery(id+"F0.imprint","IMPRINT",EDGE,{"derivedFrom":subQ5}),-1.0]])]});}
            var Q34;
            {var subQ0=sQuery(id+"F0.wireOp",EDGE,"E73.bottom");var subQ1=sQuery(id+"F0.wireOp",EDGE,"E33.right");var subQ2=makeQuery(id+"F0.imprint","INTERSECT",VERTEX,{"derivedFrom":[subQ1,subQ0]});Q34=makeQuery(id+"F0.imprint","IMPRINT",FACE,{"disambiguationData":[TD([[makeQuery(id+"F0.imprint","IMPRINT",EDGE,{"disambiguationData":[TD([[subQ2,-1.0]])],"derivedFrom":subQ1}),1.0]])]});}
            var Q35;
            {var subQ5=sQuery(id+"F0.wireOp",EDGE,"E73.left");Q35=makeQuery(id+"F0.imprint","IMPRINT",FACE,{"disambiguationData":[TD([[makeQuery(id+"F0.imprint","IMPRINT",EDGE,{"derivedFrom":subQ5}),1.0]])]});}
            var Q36;
            {var subQ5=sQuery(id+"F0.wireOp",EDGE,"E73.left");Q36=makeQuery(id+"F0.imprint","IMPRINT",FACE,{"disambiguationData":[TD([[makeQuery(id+"F0.imprint","IMPRINT",EDGE,{"derivedFrom":subQ5}),-1.0]])]});}
            var Q37;
            {var subQ12=sQuery(id+"F0.wireOp",EDGE,"E72.right");Q37=makeQuery(id+"F0.imprint","IMPRINT",FACE,{"disambiguationData":[TD([[makeQuery(id+"F0.imprint","IMPRINT",EDGE,{"derivedFrom":subQ12}),1.0]])]});}
            var Q38;
            {var subQ5=sQuery(id+"F0.wireOp",EDGE,"E72.right");Q38=makeQuery(id+"F0.imprint","IMPRINT",FACE,{"disambiguationData":[TD([[makeQuery(id+"F0.imprint","IMPRINT",EDGE,{"derivedFrom":subQ5}),-1.0]])]});}
            var Q39;
            {var subQ0=sQuery(id+"F0.wireOp",EDGE,"E32.bottom");Q39=makeQuery(id+"F0.imprint","IMPRINT",FACE,{"disambiguationData":[TD([[makeQuery(id+"F0.imprint","IMPRINT",EDGE,{"derivedFrom":subQ0}),-1.0]])]});}
            var Q40;
            {var subQ5=sQuery(id+"F0.wireOp",EDGE,"E72.left");Q40=makeQuery(id+"F0.imprint","IMPRINT",FACE,{"disambiguationData":[TD([[makeQuery(id+"F0.imprint","IMPRINT",EDGE,{"derivedFrom":subQ5}),1.0]])]});}
            var Q41;
            {var subQ1=sQuery(id+"F0.wireOp",EDGE,"E30.right");Q41=makeQuery(id+"F0.imprint","IMPRINT",FACE,{"disambiguationData":[TD([[makeQuery(id+"F0.imprint","IMPRINT",EDGE,{"derivedFrom":subQ1}),1.0]])]});}
            var Q42;
            {var subQ0=sQuery(id+"F0.wireOp",EDGE,"E30.right");Q42=makeQuery(id+"F0.imprint","IMPRINT",FACE,{"disambiguationData":[TD([[makeQuery(id+"F0.imprint","IMPRINT",EDGE,{"derivedFrom":subQ0}),-1.0]])]});}
            var Q43;
            {var subQ0=sQuery(id+"F0.wireOp",EDGE,"E30.bottom");var subQ1=sQuery(id+"F0.wireOp",EDGE,"E29.right");var subQ2=makeQuery(id+"F0.imprint","INTERSECT",VERTEX,{"derivedFrom":[subQ1,subQ0]});Q43=makeQuery(id+"F0.imprint","IMPRINT",FACE,{"disambiguationData":[TD([[makeQuery(id+"F0.imprint","IMPRINT",EDGE,{"disambiguationData":[TD([[subQ2,-1.0]])],"derivedFrom":subQ1}),1.0]])]});}
            var Q44;
            {var subQ5=sQuery(id+"F0.wireOp",EDGE,"E30.left");Q44=makeQuery(id+"F0.imprint","IMPRINT",FACE,{"disambiguationData":[TD([[makeQuery(id+"F0.imprint","IMPRINT",EDGE,{"derivedFrom":subQ5}),1.0]])]});}
            var Q45;
            {var subQ11=sQuery(id+"F0.wireOp",EDGE,"E29.bottom");Q45=makeQuery(id+"F0.imprint","IMPRINT",FACE,{"disambiguationData":[TD([[makeQuery(id+"F0.imprint","IMPRINT",EDGE,{"derivedFrom":subQ11}),-1.0]])]});}
            var Q46;
            {var subQ0=sQuery(id+"F0.wireOp",EDGE,"E71.bottom");var subQ1=sQuery(id+"F0.wireOp",EDGE,"E27.right");var subQ2=makeQuery(id+"F0.imprint","INTERSECT",VERTEX,{"derivedFrom":[subQ1,subQ0]});Q46=makeQuery(id+"F0.imprint","IMPRINT",FACE,{"disambiguationData":[TD([[makeQuery(id+"F0.imprint","IMPRINT",EDGE,{"disambiguationData":[TD([[subQ2,-1.0]])],"derivedFrom":subQ1}),1.0]])]});}
            var Q47;
            {var subQ5=sQuery(id+"F0.wireOp",EDGE,"E71.left");Q47=makeQuery(id+"F0.imprint","IMPRINT",FACE,{"disambiguationData":[TD([[makeQuery(id+"F0.imprint","IMPRINT",EDGE,{"derivedFrom":subQ5}),1.0]])]});}
            var Q48;
            {var subQ12=sQuery(id+"F0.wireOp",EDGE,"E71.left");Q48=makeQuery(id+"F0.imprint","IMPRINT",FACE,{"disambiguationData":[TD([[makeQuery(id+"F0.imprint","IMPRINT",EDGE,{"derivedFrom":subQ12}),-1.0]])]});}
            var Q49;
            {var subQ5=sQuery(id+"F0.wireOp",EDGE,"E28.bottom");Q49=makeQuery(id+"F0.imprint","IMPRINT",FACE,{"disambiguationData":[TD([[makeQuery(id+"F0.imprint","IMPRINT",EDGE,{"derivedFrom":subQ5}),-1.0]])]});}
            var Q50;
            {var subQ5=sQuery(id+"F0.wireOp",EDGE,"E28.top");Q50=makeQuery(id+"F0.imprint","IMPRINT",FACE,{"disambiguationData":[TD([[makeQuery(id+"F0.imprint","IMPRINT",EDGE,{"derivedFrom":subQ5}),1.0]])]});}
            var Q51;
            {var subQ5=sQuery(id+"F0.wireOp",EDGE,"E71.right");Q51=makeQuery(id+"F0.imprint","IMPRINT",FACE,{"disambiguationData":[TD([[makeQuery(id+"F0.imprint","IMPRINT",EDGE,{"derivedFrom":subQ5}),-1.0]])]});}
            var Q52;
            {var subQ5=sQuery(id+"F0.wireOp",EDGE,"E70.right");Q52=makeQuery(id+"F0.imprint","IMPRINT",FACE,{"disambiguationData":[TD([[makeQuery(id+"F0.imprint","IMPRINT",EDGE,{"derivedFrom":subQ5}),1.0]])]});}
            var Q53;
            {var subQ5=sQuery(id+"F0.wireOp",EDGE,"E70.right");Q53=makeQuery(id+"F0.imprint","IMPRINT",FACE,{"disambiguationData":[TD([[makeQuery(id+"F0.imprint","IMPRINT",EDGE,{"derivedFrom":subQ5}),-1.0]])]});}
            var Q54;
            {var subQ5=sQuery(id+"F0.wireOp",EDGE,"E70.left");Q54=makeQuery(id+"F0.imprint","IMPRINT",FACE,{"disambiguationData":[TD([[makeQuery(id+"F0.imprint","IMPRINT",EDGE,{"derivedFrom":subQ5}),1.0]])]});}
            var Q55;
            Q55=makeQuery(id+"F0.imprint","IMPRINT",FACE,{"disambiguationData":[TD([[makeQuery(id+"F0.imprint","IMPRINT",EDGE,{"derivedFrom":sQuery(id+"F0.wireOp",EDGE,"E13")}),1.0]])]});
            var Q56;
            {var subQ0=sQuery(id+"F0.wireOp",EDGE,"E69.right");Q56=makeQuery(id+"F0.imprint","IMPRINT",FACE,{"disambiguationData":[TD([[makeQuery(id+"F0.imprint","IMPRINT",EDGE,{"derivedFrom":subQ0}),-1.0]])]});}
            var Q57;
            {var subQ0=sQuery(id+"F0.wireOp",EDGE,"E69.left");Q57=makeQuery(id+"F0.imprint","IMPRINT",FACE,{"disambiguationData":[TD([[makeQuery(id+"F0.imprint","IMPRINT",EDGE,{"derivedFrom":subQ0}),1.0]])]});}
            var Q58;
            {var subQ1=sQuery(id+"F0.wireOp",EDGE,"E11.top");Q58=makeQuery(id+"F0.imprint","IMPRINT",FACE,{"disambiguationData":[TD([[makeQuery(id+"F0.imprint","IMPRINT",EDGE,{"derivedFrom":subQ1}),1.0]])]});}
            var Q59;
            {var subQ5=sQuery(id+"F0.wireOp",EDGE,"E11.bottom");Q59=makeQuery(id+"F0.imprint","IMPRINT",FACE,{"disambiguationData":[TD([[makeQuery(id+"F0.imprint","IMPRINT",EDGE,{"derivedFrom":subQ5}),-1.0]])]});}
            var Q60;
            {var subQ0=sQuery(id+"F0.wireOp",EDGE,"E10.bottom");var subQ1=sQuery(id+"F0.wireOp",EDGE,"E9.right");var subQ2=makeQuery(id+"F0.imprint","INTERSECT",VERTEX,{"derivedFrom":[subQ1,subQ0]});Q60=makeQuery(id+"F0.imprint","IMPRINT",FACE,{"disambiguationData":[TD([[makeQuery(id+"F0.imprint","IMPRINT",EDGE,{"disambiguationData":[TD([[subQ2,1.0]])],"derivedFrom":subQ1}),1.0]])]});}
            var Q61;
            {var subQ5=sQuery(id+"F0.wireOp",EDGE,"E10.left");Q61=makeQuery(id+"F0.imprint","IMPRINT",FACE,{"disambiguationData":[TD([[makeQuery(id+"F0.imprint","IMPRINT",EDGE,{"derivedFrom":subQ5}),-1.0]])]});}
            var Q62;
            {var subQ5=sQuery(id+"F0.wireOp",EDGE,"E9.bottom");Q62=makeQuery(id+"F0.imprint","IMPRINT",FACE,{"disambiguationData":[TD([[makeQuery(id+"F0.imprint","IMPRINT",EDGE,{"derivedFrom":subQ5}),-1.0]])]});}
            var Q63;
            {var subQ5=sQuery(id+"F0.wireOp",EDGE,"E12.left");Q63=makeQuery(id+"F0.imprint","IMPRINT",FACE,{"disambiguationData":[TD([[makeQuery(id+"F0.imprint","IMPRINT",EDGE,{"derivedFrom":subQ5}),1.0]])]});}
            var Q64;
            {var subQ5=sQuery(id+"F0.wireOp",EDGE,"E12.right");Q64=makeQuery(id+"F0.imprint","IMPRINT",FACE,{"disambiguationData":[TD([[makeQuery(id+"F0.imprint","IMPRINT",EDGE,{"derivedFrom":subQ5}),-1.0]])]});}
            var Q65;
            {var subQ5=sQuery(id+"F0.wireOp",EDGE,"E68.right");Q65=makeQuery(id+"F0.imprint","IMPRINT",FACE,{"disambiguationData":[TD([[makeQuery(id+"F0.imprint","IMPRINT",EDGE,{"derivedFrom":subQ5}),-1.0]])]});}
            var Q66;
            {var subQ0=sQuery(id+"F0.wireOp",EDGE,"E68.bottom");var subQ1=sQuery(id+"F0.wireOp",EDGE,"E8.right");var subQ2=makeQuery(id+"F0.imprint","INTERSECT",VERTEX,{"derivedFrom":[subQ1,subQ0]});Q66=makeQuery(id+"F0.imprint","IMPRINT",FACE,{"disambiguationData":[TD([[makeQuery(id+"F0.imprint","IMPRINT",EDGE,{"disambiguationData":[TD([[subQ2,-1.0]])],"derivedFrom":subQ1}),1.0]])]});}
            var Q67;
            {var subQ5=sQuery(id+"F0.wireOp",EDGE,"E68.left");Q67=makeQuery(id+"F0.imprint","IMPRINT",FACE,{"disambiguationData":[TD([[makeQuery(id+"F0.imprint","IMPRINT",EDGE,{"derivedFrom":subQ5}),1.0]])]});}
            var Q68;
            {var subQ10=sQuery(id+"F0.wireOp",EDGE,"E68.left");Q68=makeQuery(id+"F0.imprint","IMPRINT",FACE,{"disambiguationData":[TD([[makeQuery(id+"F0.imprint","IMPRINT",EDGE,{"derivedFrom":subQ10}),-1.0]])]});}
            var Q69;
            {var subQ0=sQuery(id+"F0.wireOp",EDGE,"E7.top");Q69=makeQuery(id+"F0.imprint","IMPRINT",FACE,{"disambiguationData":[TD([[makeQuery(id+"F0.imprint","IMPRINT",EDGE,{"derivedFrom":subQ0}),-1.0]])]});}
            var Q70;
            {var subQ0=sQuery(id+"F0.wireOp",EDGE,"E7.left");var subQ1=sQuery(id+"F0.wireOp",EDGE,"E6.top");var subQ2=makeQuery(id+"F0.imprint","INTERSECT",VERTEX,{"derivedFrom":[subQ1,subQ0]});Q70=makeQuery(id+"F0.imprint","IMPRINT",FACE,{"disambiguationData":[TD([[makeQuery(id+"F0.imprint","IMPRINT",EDGE,{"disambiguationData":[TD([[subQ2,1.0]])],"derivedFrom":subQ1}),-1.0]])]});}
            var Q71;
            {var subQ5=sQuery(id+"F0.wireOp",EDGE,"E7.bottom");Q71=makeQuery(id+"F0.imprint","IMPRINT",FACE,{"disambiguationData":[TD([[makeQuery(id+"F0.imprint","IMPRINT",EDGE,{"derivedFrom":subQ5}),1.0]])]});}
            var Q72;
            {var subQ0=sQuery(id+"F0.wireOp",EDGE,"E6.bottom");var subQ1=sQuery(id+"F0.wireOp",EDGE,"E5.right");var subQ2=makeQuery(id+"F0.imprint","INTERSECT",VERTEX,{"derivedFrom":[subQ1,subQ0]});Q72=makeQuery(id+"F0.imprint","IMPRINT",FACE,{"disambiguationData":[TD([[makeQuery(id+"F0.imprint","IMPRINT",EDGE,{"disambiguationData":[TD([[subQ2,1.0]])],"derivedFrom":subQ1}),-1.0]])]});}
            var Q73;
            {var subQ5=sQuery(id+"F0.wireOp",EDGE,"E6.left");Q73=makeQuery(id+"F0.imprint","IMPRINT",FACE,{"disambiguationData":[TD([[makeQuery(id+"F0.imprint","IMPRINT",EDGE,{"derivedFrom":subQ5}),1.0]])]});}
            var Q74;
            {var subQ3=sQuery(id+"F0.wireOp",EDGE,"E8.bottom");var subQ5=sQuery(id+"F0.wireOp",EDGE,"E5.right");var subQ6=makeQuery(id+"F0.imprint","INTERSECT",VERTEX,{"derivedFrom":[subQ5,subQ3]});Q74=makeQuery(id+"F0.imprint","IMPRINT",FACE,{"disambiguationData":[TD([[makeQuery(id+"F0.imprint","IMPRINT",EDGE,{"disambiguationData":[TD([[subQ6,-1.0]])],"derivedFrom":subQ5}),1.0]])]});}
            var Q75;
            {var subQ5=sQuery(id+"F0.wireOp",EDGE,"E8.left");Q75=makeQuery(id+"F0.imprint","IMPRINT",FACE,{"disambiguationData":[TD([[makeQuery(id+"F0.imprint","IMPRINT",EDGE,{"derivedFrom":subQ5}),1.0]])]});}
            var Q76;
            {var subQ0=sQuery(id+"F0.wireOp",EDGE,"E8.top");var subQ1=sQuery(id+"F0.wireOp",EDGE,"E5.right");var subQ2=makeQuery(id+"F0.imprint","INTERSECT",VERTEX,{"derivedFrom":[subQ1,subQ0]});Q76=makeQuery(id+"F0.imprint","IMPRINT",FACE,{"disambiguationData":[TD([[makeQuery(id+"F0.imprint","IMPRINT",EDGE,{"disambiguationData":[TD([[subQ2,-1.0]])],"derivedFrom":subQ1}),-1.0]])]});}
            var Q77;
            {var subQ5=sQuery(id+"F0.wireOp",EDGE,"E5.bottom");Q77=makeQuery(id+"F0.imprint","IMPRINT",FACE,{"disambiguationData":[TD([[makeQuery(id+"F0.imprint","IMPRINT",EDGE,{"derivedFrom":subQ5}),1.0]])]});}
            var Q78;
            {var subQ5=sQuery(id+"F0.wireOp",EDGE,"E67.right");Q78=makeQuery(id+"F0.imprint","IMPRINT",FACE,{"disambiguationData":[TD([[makeQuery(id+"F0.imprint","IMPRINT",EDGE,{"derivedFrom":subQ5}),-1.0]])]});}
            var Q79;
            {var subQ5=sQuery(id+"F0.wireOp",EDGE,"E67.left");Q79=makeQuery(id+"F0.imprint","IMPRINT",FACE,{"disambiguationData":[TD([[makeQuery(id+"F0.imprint","IMPRINT",EDGE,{"derivedFrom":subQ5}),1.0]])]});}
            var Q80;
            {var subQ0=sQuery(id+"F0.wireOp",EDGE,"E4.right");Q80=makeQuery(id+"F0.imprint","IMPRINT",FACE,{"disambiguationData":[TD([[makeQuery(id+"F0.imprint","IMPRINT",EDGE,{"derivedFrom":subQ0}),1.0]])]});}
            var Q81;
            {var subQ5=sQuery(id+"F0.wireOp",EDGE,"E4.left");Q81=makeQuery(id+"F0.imprint","IMPRINT",FACE,{"disambiguationData":[TD([[makeQuery(id+"F0.imprint","IMPRINT",EDGE,{"derivedFrom":subQ5}),-1.0]])]});}
            var Q82;
            {var subQ1=sQuery(id+"F0.wireOp",EDGE,"E3.bottom");Q82=makeQuery(id+"F0.imprint","IMPRINT",FACE,{"disambiguationData":[TD([[makeQuery(id+"F0.imprint","IMPRINT",EDGE,{"derivedFrom":subQ1}),-1.0]])]});}
            var Q83;
            {var subQ5=sQuery(id+"F0.wireOp",EDGE,"E66.right");Q83=makeQuery(id+"F0.imprint","IMPRINT",FACE,{"disambiguationData":[TD([[makeQuery(id+"F0.imprint","IMPRINT",EDGE,{"derivedFrom":subQ5}),-1.0]])]});}
            var Q84;
            {var subQ0=sQuery(id+"F0.wireOp",EDGE,"E66.bottom");var subQ1=sQuery(id+"F0.wireOp",EDGE,"E1.right");var subQ2=makeQuery(id+"F0.imprint","INTERSECT",VERTEX,{"derivedFrom":[subQ1,subQ0]});Q84=makeQuery(id+"F0.imprint","IMPRINT",FACE,{"disambiguationData":[TD([[makeQuery(id+"F0.imprint","IMPRINT",EDGE,{"disambiguationData":[TD([[subQ2,-1.0]])],"derivedFrom":subQ1}),1.0]])]});}
            var Q85;
            {var subQ5=sQuery(id+"F0.wireOp",EDGE,"E66.left");Q85=makeQuery(id+"F0.imprint","IMPRINT",FACE,{"disambiguationData":[TD([[makeQuery(id+"F0.imprint","IMPRINT",EDGE,{"derivedFrom":subQ5}),1.0]])]});}
            var Q86;
            {var subQ0=sQuery(id+"F0.wireOp",EDGE,"E0.bottom");Q86=makeQuery(id+"F0.imprint","IMPRINT",FACE,{"disambiguationData":[TD([[makeQuery(id+"F0.imprint","IMPRINT",EDGE,{"derivedFrom":subQ0}),1.0]])]});}
            var Q87;
            {var subQ5=sQuery(id+"F0.wireOp",EDGE,"E2.right");Q87=makeQuery(id+"F0.imprint","IMPRINT",FACE,{"disambiguationData":[TD([[makeQuery(id+"F0.imprint","IMPRINT",EDGE,{"derivedFrom":subQ5}),-1.0]])]});}
            var Q88;
            {var subQ5=sQuery(id+"F0.wireOp",EDGE,"E2.left");Q88=makeQuery(id+"F0.imprint","IMPRINT",FACE,{"disambiguationData":[TD([[makeQuery(id+"F0.imprint","IMPRINT",EDGE,{"derivedFrom":subQ5}),1.0]])]});}
            var Q89;
            {var subQ3=sQuery(id+"F0.wireOp",EDGE,"E2.bottom");var subQ5=sQuery(id+"F0.wireOp",EDGE,"E0.right");var subQ6=makeQuery(id+"F0.imprint","INTERSECT",VERTEX,{"derivedFrom":[subQ5,subQ3]});Q89=makeQuery(id+"F0.imprint","IMPRINT",FACE,{"disambiguationData":[TD([[makeQuery(id+"F0.imprint","IMPRINT",EDGE,{"disambiguationData":[TD([[subQ6,-1.0]])],"derivedFrom":subQ5}),1.0]])]});}
            var Q90;
            {var subQ5=sQuery(id+"F0.wireOp",EDGE,"E1.left");Q90=makeQuery(id+"F0.imprint","IMPRINT",FACE,{"disambiguationData":[TD([[makeQuery(id+"F0.imprint","IMPRINT",EDGE,{"derivedFrom":subQ5}),1.0]])]});}
            var Q91;
            {var subQ9=sQuery(id+"F0.wireOp",EDGE,"E66.left");Q91=makeQuery(id+"F0.imprint","IMPRINT",FACE,{"disambiguationData":[TD([[makeQuery(id+"F0.imprint","IMPRINT",EDGE,{"derivedFrom":subQ9}),-1.0]])]});}
            extrude(context, id + "F1", {"entities" : qUnion([Q0, Q1, Q2, Q3, Q4, Q5, Q6, Q7, Q8, Q9, Q10, Q11, Q12, Q13, Q14, Q15, Q16, Q17, Q18, Q19, Q20, Q21, Q22, Q23, Q24, Q25, Q26, Q27, Q28, Q29, Q30, Q31, Q32, Q33, Q34, Q35, Q36, Q37, Q38, Q39, Q40, Q41, Q42, Q43, Q44, Q45, Q46, Q47, Q48, Q49, Q50, Q51, Q52, Q53, Q54, Q55, Q56, Q57, Q58, Q59, Q60, Q61, Q62, Q63, Q64, Q65, Q66, Q67, Q68, Q69, Q70, Q71, Q72, Q73, Q74, Q75, Q76, Q77, Q78, Q79, Q80, Q81, Q82, Q83, Q84, Q85, Q86, Q87, Q88, Q89, Q90, Q91]), "depth" : 25.4 * mm, "offsetDistance" : 25.4 * mm});
        }
    });
